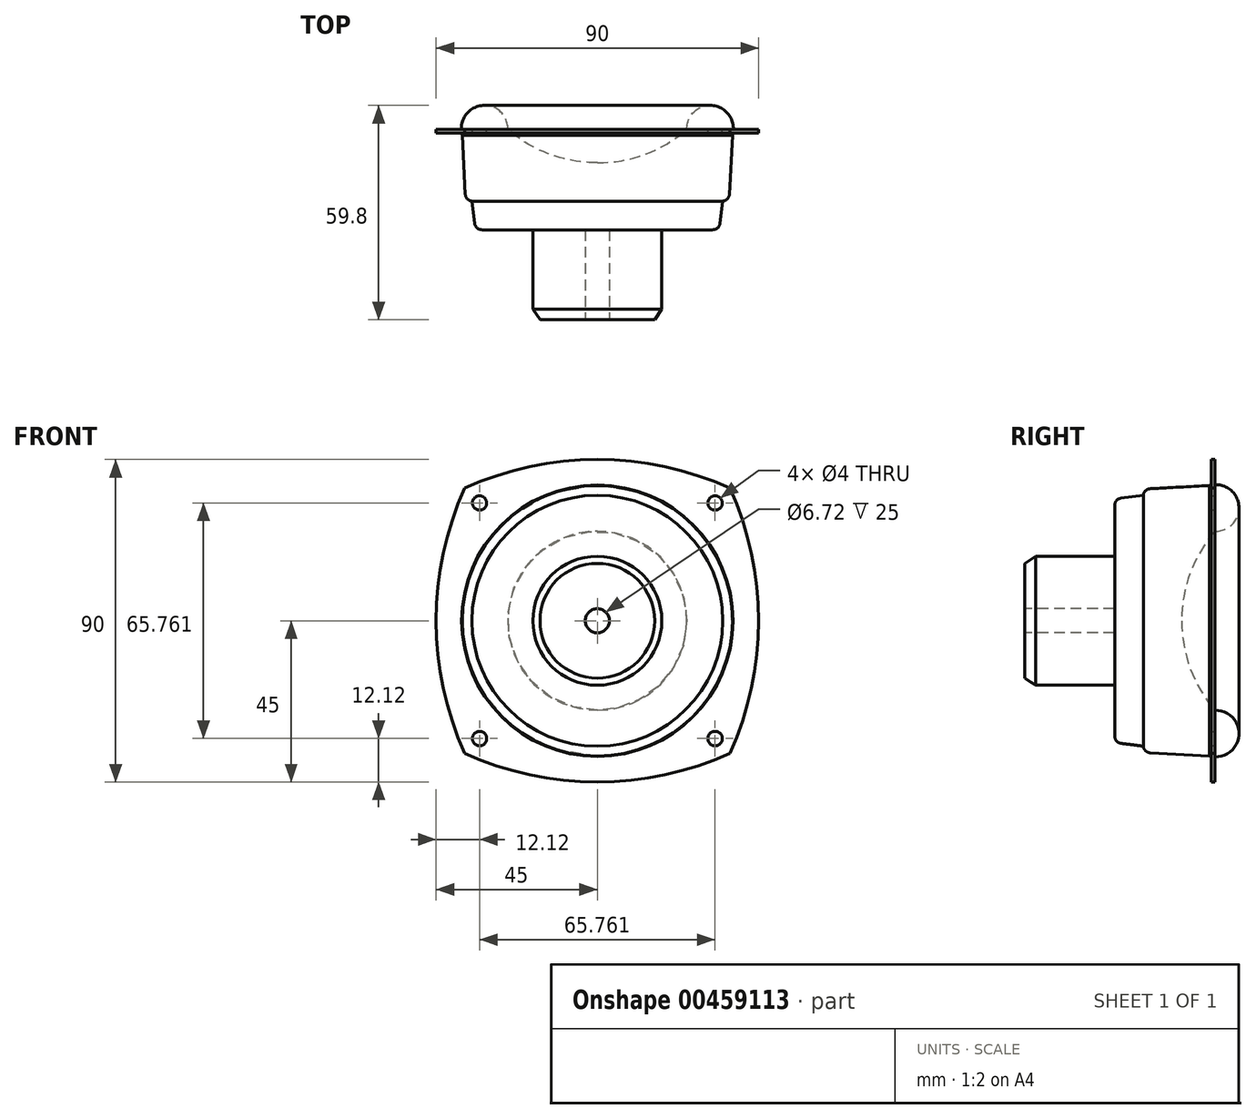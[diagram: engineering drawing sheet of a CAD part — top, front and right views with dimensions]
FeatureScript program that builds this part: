
annotation { "Feature Type Name" : "Feature", "Feature Type Description" : "" }
export const myFeature = defineFeature(function(context is Context, id is Id, definition is map)
    precondition{}
    {
        {
            var Q0;
            Q0=qCreatedBy(makeId("Front.planeOp"),FACE);
            var sketch = newSketch(context, id + "F0", { "sketchPlane" : qUnion([Q0])});
            skLineSegment(sketch, "E0", {"start": v(-56.36, 0) * mm, "end": v(56.36, 0) * mm, "construction": true});
            skLineSegment(sketch, "E1", {"start": v(56.36, 0) * mm, "end": v(56.36, 0) * mm});
            skLineSegment(sketch, "E2.bottom", {"start": v(-45, 45) * mm, "end": v(45, 45) * mm, "construction": true});
            skLineSegment(sketch, "E2.top", {"start": v(-45, -45) * mm, "end": v(45, -45) * mm, "construction": true});
            skLineSegment(sketch, "E2.left", {"start": v(-45, 45) * mm, "end": v(-45, -45) * mm, "construction": true});
            skLineSegment(sketch, "E2.right", {"start": v(45, 45) * mm, "end": v(45, -45) * mm, "construction": true});
            skArc(sketch, "E3", {"start": v(37.03, 37.03) * mm, "mid": v(0, 45) * mm, "end": v(-37.03, 37.03) * mm});
            skArc(sketch, "E4.1.0", {"start": v(-37.03, 37.03) * mm, "mid": v(-45, 0) * mm, "end": v(-37.03, -37.03) * mm});
            skArc(sketch, "E4.2.0", {"start": v(-37.03, -37.03) * mm, "mid": v(0, -45) * mm, "end": v(37.03, -37.03) * mm});
            skArc(sketch, "E4.3.0", {"start": v(37.03, -37.03) * mm, "mid": v(45, 0) * mm, "end": v(37.03, 37.03) * mm});
            skPoint(sketch, "E4.center", {"position": v(0, 0) * mm});
            skSolve(sketch);
        }
        {
            var Q0;
            Q0 = qSketchRegion(id + "F0", true);
            extrude(context, id + "F1", {"entities" : qUnion([Q0]), "depth" : 1 * mm});
        }
        {
            var Q0;
            Q0=makeQuery(id+"F1.opExtrude","CAP_FACE",FACE,{"disambiguationData":[OSD([sQuery(id+"F0.wireOp",EDGE,"E3"),sQuery(id+"F0.wireOp",EDGE,"E4.1.0"),sQuery(id+"F0.wireOp",EDGE,"E4.2.0"),sQuery(id+"F0.wireOp",EDGE,"E4.3.0")])],"isStart":false});
            var sketch = newSketch(context, id + "F2", { "sketchPlane" : qUnion([Q0])});
            skCircle(sketch, "E5", {"center": v(0, 0) * mm, "radius": 37.75 * mm});
            skSolve(sketch);
        }
        {
            var Q0;
            Q0 = qSketchRegion(id + "F2", true);
            extrude(context, id + "F3", {"entities" : qUnion([Q0]), "operationType" : NewBodyOperationType.ADD, "depth" : 19 * mm});
        }
        {
            var Q0;
            Q0=makeQuery(id+"F3.opExtrude","CAP_EDGE",EDGE,{"disambiguationData":[OSD([sQuery(id+"F2.wireOp",EDGE,"E5")])],"isStart":false});
            chamfer(context, id + "F4", {"entities" : qUnion([Q0]), "chamferType" : ChamferType.TWO_OFFSETS, "width1" : 1 * mm, "oppositeDirection" : false, "width2" : 19 * mm, "tangentPropagation" : true});
        }
        {
            var Q0;
            Q0=makeQuery(id+"F3.opExtrude","CAP_FACE",FACE,{"disambiguationData":[OSD([sQuery(id+"F2.wireOp",EDGE,"E5")])],"isStart":false});
            var sketch = newSketch(context, id + "F5", { "sketchPlane" : qUnion([Q0])});
            skCircle(sketch, "E6", {"center": v(0, 0) * mm, "radius": 35 * mm});
            skSolve(sketch);
        }
        {
            var Q0;
            Q0 = qSketchRegion(id + "F5", true);
            extrude(context, id + "F6", {"entities" : qUnion([Q0]), "operationType" : NewBodyOperationType.ADD, "depth" : 8 * mm});
        }
        {
            var Q0;
            Q0=makeQuery(id+"F6.opExtrude","CAP_EDGE",EDGE,{"disambiguationData":[OSD([sQuery(id+"F5.wireOp",EDGE,"E6")])],"isStart":false});
            chamfer(context, id + "F7", {"entities" : qUnion([Q0]), "chamferType" : ChamferType.TWO_OFFSETS, "width1" : 1 * mm, "oppositeDirection" : false, "width2" : 8 * mm, "tangentPropagation" : true});
        }
        {
            var Q0;
            {var subQ0=sQuery(id+"F2.wireOp",EDGE,"E5");Q0=makeQuery(id+"F4.opChamfer","BLEND_EDGE",EDGE,{"blendedFrom":[makeQuery(id+"F3.opExtrude","CAP_EDGE",EDGE,{"disambiguationData":[OSD([subQ0])],"isStart":false}),makeQuery(id+"F3.opExtrude","CAP_FACE",FACE,{"disambiguationData":[OSD([subQ0])],"isStart":false})],"blendedInto":[makeQuery(id+"F3.opExtrude","CAP_FACE",FACE,{"disambiguationData":[OSD([subQ0])],"isStart":false})]});}
            fillet(context, id + "F8", {"entities" : qUnion([Q0]), "radius" : 2 * mm, "tangentPropagation" : true, "allowEdgeOverflow" : false});
        }
        {
            var Q0;
            {var subQ0=sQuery(id+"F5.wireOp",EDGE,"E6");Q0=makeQuery(id+"F7.opChamfer","BLEND_EDGE",EDGE,{"blendedFrom":[makeQuery(id+"F6.opExtrude","CAP_EDGE",EDGE,{"disambiguationData":[OSD([subQ0])],"isStart":false}),makeQuery(id+"F6.opExtrude","CAP_FACE",FACE,{"disambiguationData":[OSD([subQ0])],"isStart":false})],"blendedInto":[makeQuery(id+"F6.opExtrude","CAP_FACE",FACE,{"disambiguationData":[OSD([subQ0])],"isStart":false})]});}
            fillet(context, id + "F9", {"entities" : qUnion([Q0]), "radius" : 2 * mm, "tangentPropagation" : true, "allowEdgeOverflow" : false});
        }
        {
            var Q0;
            Q0=makeQuery(id+"F6.opExtrude","CAP_FACE",FACE,{"disambiguationData":[OSD([sQuery(id+"F5.wireOp",EDGE,"E6")])],"isStart":false});
            var sketch = newSketch(context, id + "F10", { "sketchPlane" : qUnion([Q0])});
            skCircle(sketch, "E7", {"center": v(0, 0) * mm, "radius": 18 * mm});
            skSolve(sketch);
        }
        {
            var Q0;
            Q0 = qSketchRegion(id + "F10", true);
            extrude(context, id + "F11", {"entities" : qUnion([Q0]), "operationType" : NewBodyOperationType.ADD, "depth" : 25.1 * mm});
        }
        {
            var Q0;
            Q0=makeQuery(id+"F11.opExtrude","CAP_EDGE",EDGE,{"disambiguationData":[OSD([sQuery(id+"F10.wireOp",EDGE,"E7")])],"isStart":false});
            chamfer(context, id + "F12", {"entities" : qUnion([Q0]), "chamferType" : ChamferType.TWO_OFFSETS, "width1" : 2 * mm, "oppositeDirection" : false, "width2" : 3 * mm, "tangentPropagation" : true});
        }
        {
            var Q0;
            Q0=makeQuery(id+"F11.opExtrude","CAP_FACE",FACE,{"disambiguationData":[OSD([sQuery(id+"F10.wireOp",EDGE,"E7")])],"isStart":false});
            var sketch = newSketch(context, id + "F13", { "sketchPlane" : qUnion([Q0])});
            skCircle(sketch, "E8", {"center": v(0, 0) * mm, "radius": 3.36 * mm});
            skSolve(sketch);
        }
        {
            var Q0;
            Q0 = qSketchRegion(id + "F13", true);
            extrude(context, id + "F14", {"entities" : qUnion([Q0]), "operationType" : NewBodyOperationType.REMOVE, "oppositeDirection" : true, "depth" : 25 * mm});
        }
        {
            var Q0;
            Q0=makeQuery(id+"F1.opExtrude","CAP_FACE",FACE,{"disambiguationData":[OSD([sQuery(id+"F0.wireOp",EDGE,"E3"),sQuery(id+"F0.wireOp",EDGE,"E4.1.0"),sQuery(id+"F0.wireOp",EDGE,"E4.2.0"),sQuery(id+"F0.wireOp",EDGE,"E4.3.0")])],"isStart":true});
            var sketch = newSketch(context, id + "F15", { "sketchPlane" : qUnion([Q0])});
            skCircle(sketch, "E9", {"center": v(0, 0) * mm, "radius": 46.5 * mm, "construction": true});
            skLineSegment(sketch, "E10", {"start": v(0, 0) * mm, "end": v(-37.03, 37.03) * mm, "construction": true});
            skCircle(sketch, "E11", {"center": v(-32.88, 32.88) * mm, "radius": 2 * mm});
            skLineSegment(sketch, "E12.1.0", {"start": v(0, 0) * mm, "end": v(-37.03, -37.03) * mm, "construction": true});
            skCircle(sketch, "E12.1.1", {"center": v(-32.88, -32.88) * mm, "radius": 2 * mm});
            skLineSegment(sketch, "E12.2.0", {"start": v(0, 0) * mm, "end": v(37.03, -37.03) * mm, "construction": true});
            skCircle(sketch, "E12.2.1", {"center": v(32.88, -32.88) * mm, "radius": 2 * mm});
            skLineSegment(sketch, "E12.3.0", {"start": v(0, 0) * mm, "end": v(37.03, 37.03) * mm, "construction": true});
            skCircle(sketch, "E12.3.1", {"center": v(32.88, 32.88) * mm, "radius": 2 * mm});
            skSolve(sketch);
        }
        {
            var Q0;
            Q0 = qSketchRegion(id + "F15", true);
            extrude(context, id + "F16", {"entities" : qUnion([Q0]), "operationType" : NewBodyOperationType.REMOVE, "endBound" : BoundingType.THROUGH_ALL, "oppositeDirection" : true, "depth" : 25 * mm});
        }
        {
            var Q0;
            Q0=qCreatedBy(makeId("Top.planeOp"),FACE);
            var sketch = newSketch(context, id + "F17", { "sketchPlane" : qUnion([Q0])});
            skArc(sketch, "E13", {"start": v(-25, 0) * mm, "mid": v(-13.34, -6.9) * mm, "end": v(0, -9.31) * mm});
            skLineSegment(sketch, "E14", {"start": v(-25, 0) * mm, "end": v(0, 0) * mm});
            skLineSegment(sketch, "E15", {"start": v(0, 0) * mm, "end": v(0, 28.9) * mm, "construction": true});
            skLineSegment(sketch, "E16", {"start": v(0, 0) * mm, "end": v(0, -9.31) * mm});
            skSolve(sketch);
        }
        {
            var Q0;
            Q0 = qSketchRegion(id + "F17", true);
            var Q1;
            Q1=sQuery(id+"F17.wireOp",EDGE,"E15");
            revolve(context, id + "F18", {"operationType" : NewBodyOperationType.REMOVE, "entities" : qUnion([Q0]), "axis" : qUnion([Q1]), "revolveType" : RevolveType.FULL, "oppositeDirection" : true});
        }
        {
            var Q0;
            Q0=qCreatedBy(makeId("Top.planeOp"),FACE);
            var sketch = newSketch(context, id + "F19", { "sketchPlane" : qUnion([Q0])});
            skCircle(sketch, "E17", {"center": v(-31.47, 0.2) * mm, "radius": 6.5 * mm});
            skSolve(sketch);
        }
        {
            var Q0;
            Q0 = qSketchRegion(id + "F19", true);
            var Q1;
            Q1=sQuery(id+"F17.wireOp",EDGE,"E15");
            revolve(context, id + "F20", {"operationType" : NewBodyOperationType.ADD, "entities" : qUnion([Q0]), "axis" : qUnion([Q1]), "revolveType" : RevolveType.FULL});
        }
    });
